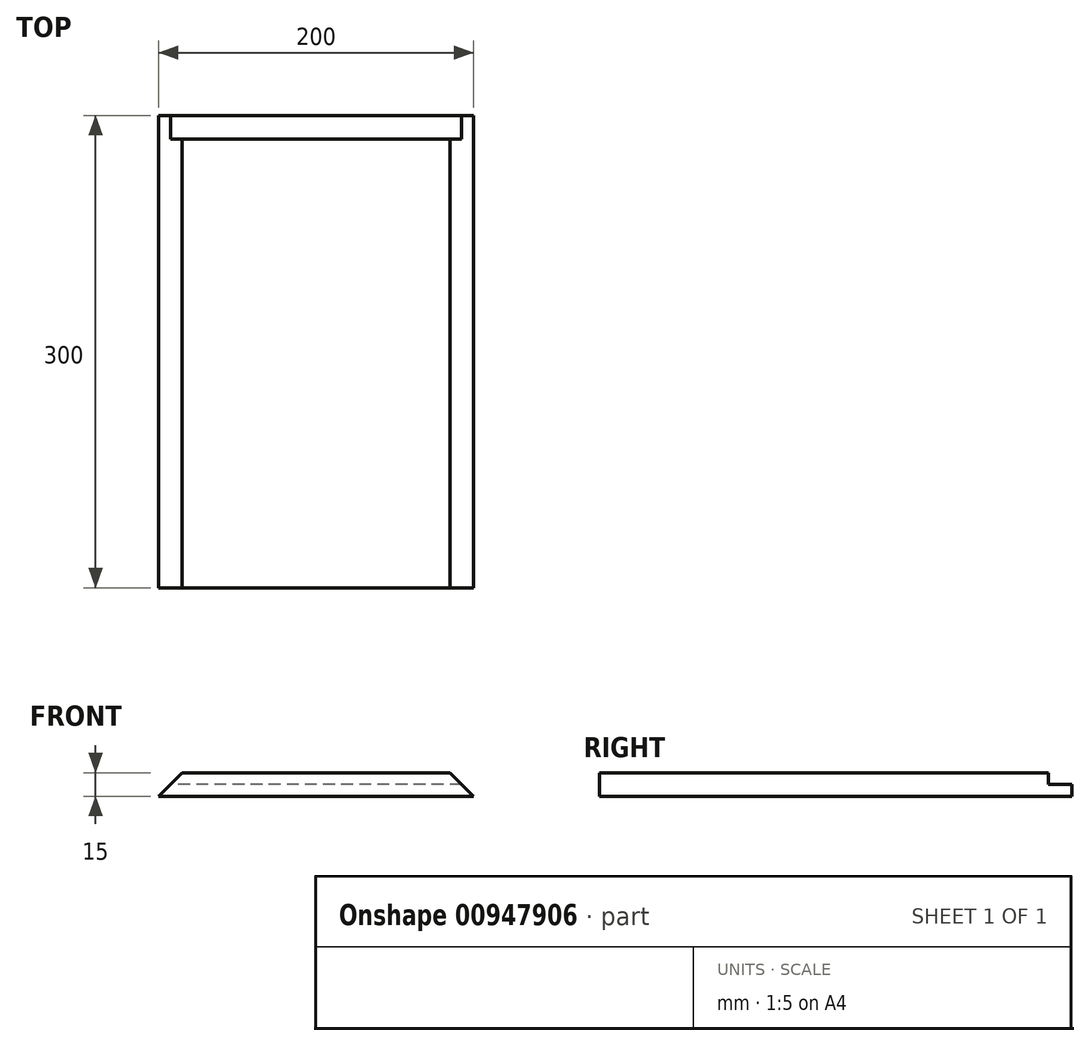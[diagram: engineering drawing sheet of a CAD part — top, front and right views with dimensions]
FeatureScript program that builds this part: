
annotation { "Feature Type Name" : "Feature", "Feature Type Description" : "" }
export const myFeature = defineFeature(function(context is Context, id is Id, definition is map)
    precondition{}
    {
        {
            var Q0;
            Q0=qCreatedBy(makeId("Right.planeOp"),FACE);
            cPlane(context, id + "F0", {"entities" : qUnion([Q0]), "cplaneType" : CPlaneType.OFFSET, "offset" : 100 * mm, "width" : 150 * mm, "height" : 150 * mm});
        }
        {
            var Q0;
            Q0=qCreatedBy(makeId("Right.planeOp"),FACE);
            cPlane(context, id + "F1", {"entities" : qUnion([Q0]), "cplaneType" : CPlaneType.OFFSET, "offset" : 100 * mm, "oppositeDirection" : true, "width" : 150 * mm, "height" : 150 * mm});
        }
        {
            var Q0;
            Q0=qCreatedBy(makeId("Front.planeOp"),FACE);
            var sketch = newSketch(context, id + "F2", { "sketchPlane" : qUnion([Q0])});
            skLineSegment(sketch, "E0", {"start": v(-100, 0) * mm, "end": v(100, 0) * mm});
            skLineSegment(sketch, "E1", {"start": v(100, 0) * mm, "end": v(85, 15) * mm});
            skLineSegment(sketch, "E2", {"start": v(85, 15) * mm, "end": v(-85, 15) * mm});
            skLineSegment(sketch, "E3", {"start": v(-85, 15) * mm, "end": v(-100, 0) * mm});
            skSolve(sketch);
        }
        {
            var Q0;
            Q0=qCreatedBy(makeId("Front.planeOp"),FACE);
            cPlane(context, id + "F3", {"entities" : qUnion([Q0]), "cplaneType" : CPlaneType.OFFSET, "offset" : 150 * mm, "width" : 150 * mm, "height" : 150 * mm});
        }
        {
            var Q0;
            Q0=qCreatedBy(makeId("Front.planeOp"),FACE);
            cPlane(context, id + "F4", {"entities" : qUnion([Q0]), "cplaneType" : CPlaneType.OFFSET, "offset" : 150 * mm, "oppositeDirection" : true, "width" : 150 * mm, "height" : 150 * mm});
        }
        {
            var Q0;
            Q0=makeQuery(id+"F2.imprint","IMPRINT",FACE,{"disambiguationData":[TD([[makeQuery(id+"F2.imprint","IMPRINT",EDGE,{"derivedFrom":sQuery(id+"F2.wireOp",EDGE,"E0")}),1.0]])]});
            var Q1;
            Q1=qCreatedBy(id+"F3.planeOp",FACE);
            var Q2;
            Q2=qCreatedBy(id+"F4.planeOp",FACE);
            extrude(context, id + "F5", {"entities" : qUnion([Q0]), "endBound" : BoundingType.UP_TO_SURFACE, "depth" : 25 * mm, "endBoundEntityFace" : qUnion([Q1]), "offsetDistance" : 25 * mm, "hasSecondDirection" : true, "secondDirectionBound" : BoundingType.UP_TO_SURFACE, "secondDirectionOppositeDirection" : true, "secondDirectionDepth" : 25 * mm, "secondDirectionBoundEntityFace" : qUnion([Q2]), "hasSecondDirectionOffset" : true, "secondDirectionOffsetDistance" : 0 * mm});
        }
        {
            var Q0;
            Q0=qCreatedBy(id+"F4.planeOp",FACE);
            var sketch = newSketch(context, id + "F6", { "sketchPlane" : qUnion([Q0])});
            skLineSegment(sketch, "E4.bottom", {"start": v(100, 20) * mm, "end": v(-100, 20) * mm});
            skLineSegment(sketch, "E4.top", {"start": v(100, 7.5) * mm, "end": v(-100, 7.5) * mm});
            skLineSegment(sketch, "E4.left", {"start": v(100, 20) * mm, "end": v(100, 7.5) * mm});
            skLineSegment(sketch, "E4.right", {"start": v(-100, 20) * mm, "end": v(-100, 7.5) * mm});
            skSolve(sketch);
        }
        {
            var Q0;
            Q0=makeQuery(id+"F6.imprint","IMPRINT",FACE,{"disambiguationData":[TD([[makeQuery(id+"F6.imprint","IMPRINT",EDGE,{"derivedFrom":sQuery(id+"F6.wireOp",EDGE,"E4.bottom")}),1.0]])]});
            extrude(context, id + "F7", {"entities" : qUnion([Q0]), "operationType" : NewBodyOperationType.REMOVE, "depth" : 15 * mm, "offsetDistance" : 25 * mm});
        }
    });
